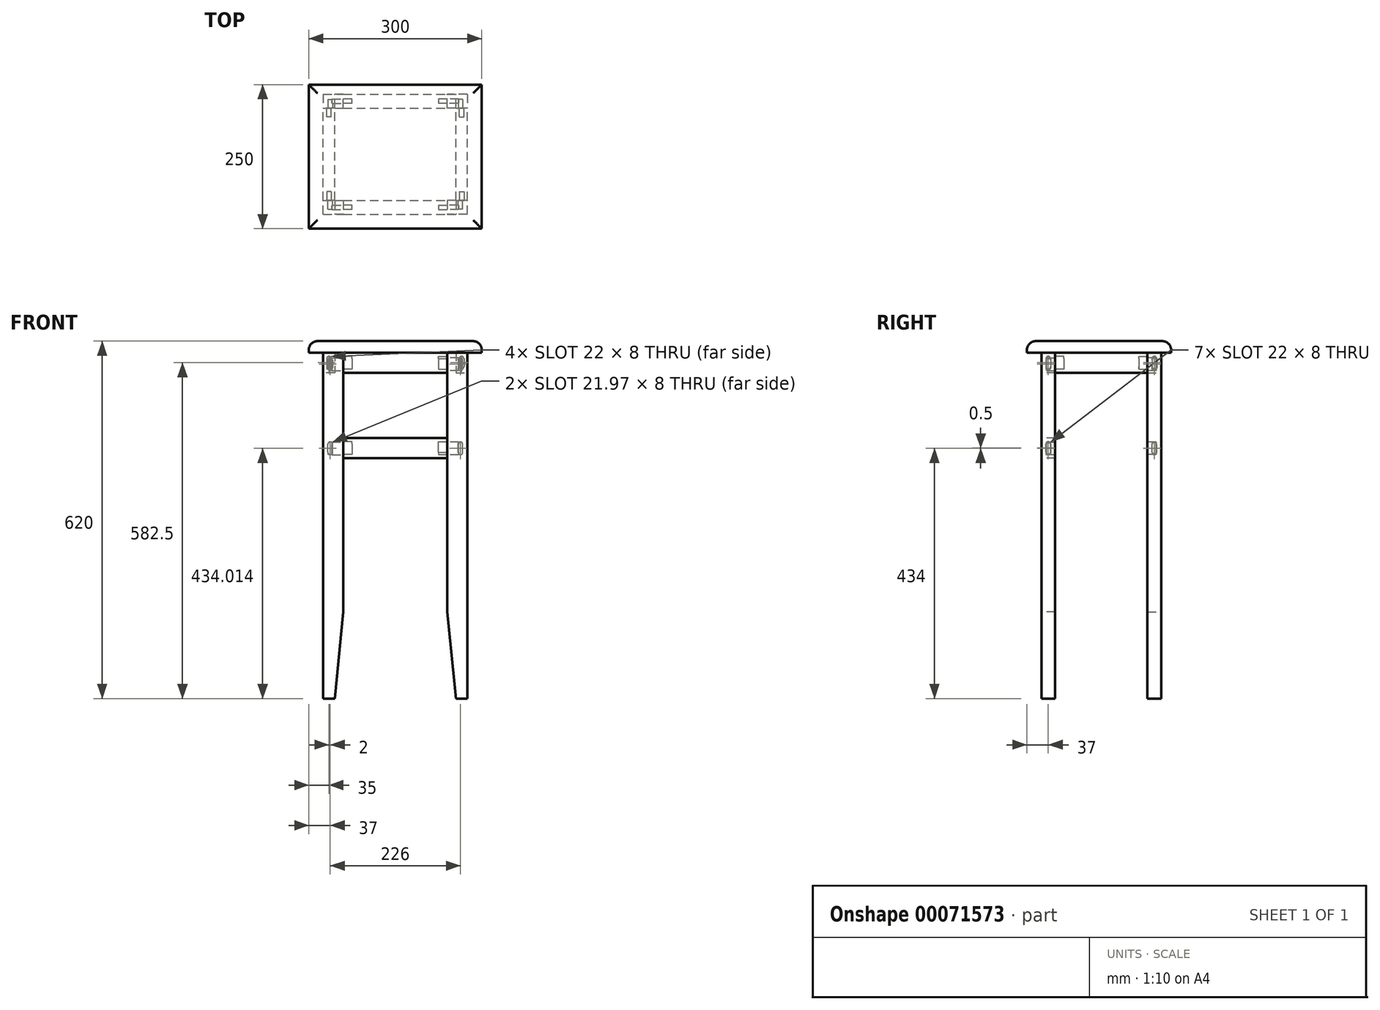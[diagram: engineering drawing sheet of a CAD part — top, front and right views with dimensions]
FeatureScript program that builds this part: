
annotation { "Feature Type Name" : "Feature", "Feature Type Description" : "" }
export const myFeature = defineFeature(function(context is Context, id is Id, definition is map)
    precondition{}
    {
        {
            var Q0;
            Q0=qCreatedBy(makeId("Top.planeOp"),FACE);
            var sketch = newSketch(context, id + "F0", { "sketchPlane" : qUnion([Q0])});
            skLineSegment(sketch, "E0.rect.bottom", {"start": v(125, -100) * mm, "end": v(-125, -100) * mm, "construction": true});
            skLineSegment(sketch, "E0.rect.top", {"start": v(125, 100) * mm, "end": v(-125, 100) * mm, "construction": true});
            skLineSegment(sketch, "E0.rect.left", {"start": v(125, -100) * mm, "end": v(125, 100) * mm, "construction": true});
            skLineSegment(sketch, "E0.rect.right", {"start": v(-125, -100) * mm, "end": v(-125, 100) * mm, "construction": true});
            skPoint(sketch, "E0.rect.middle", {"position": v(0, 0) * mm});
            skLineSegment(sketch, "E1.bottom", {"start": v(-125, -100) * mm, "end": v(-90, -100) * mm});
            skLineSegment(sketch, "E1.top", {"start": v(-125, -76) * mm, "end": v(-90, -76) * mm});
            skLineSegment(sketch, "E1.left", {"start": v(-125, -100) * mm, "end": v(-125, -76) * mm});
            skLineSegment(sketch, "E1.right", {"start": v(-90, -100) * mm, "end": v(-90, -76) * mm});
            skSolve(sketch);
        }
        {
            var Q0;
            Q0=makeQuery(id+"F0.imprint","IMPRINT",FACE,{"disambiguationData":[TD([[makeQuery(id+"F0.imprint","IMPRINT",EDGE,{"derivedFrom":sQuery(id+"F0.wireOp",EDGE,"E1.bottom")}),1.0]])]});
            extrude(context, id + "F1", {"entities" : qUnion([Q0]), "depth" : 600 * mm});
        }
        {
            var Q0;
            Q0=makeQuery(id+"F1.opExtrude","SWEPT_FACE",FACE,{"disambiguationData":[OSD([sQuery(id+"F0.wireOp",EDGE,"E1.right")])]});
            var sketch = newSketch(context, id + "F2", { "sketchPlane" : qUnion([Q0])});
            skLineSegment(sketch, "E2", {"start": v(-88, 508.7) * mm, "end": v(-88, 39.07) * mm, "construction": true});
            skPoint(sketch, "E2.startSnap0", {"position": v(-88, 600) * mm});
            skLineSegment(sketch, "E3.rect.left", {"start": v(-84, 587) * mm, "end": v(-84, 573) * mm});
            skLineSegment(sketch, "E3.rect.right", {"start": v(-92, 587) * mm, "end": v(-92, 573) * mm});
            skLineSegment(sketch, "E4.rect.left", {"start": v(-84, 427) * mm, "end": v(-84, 441) * mm});
            skLineSegment(sketch, "E4.rect.right", {"start": v(-92, 427) * mm, "end": v(-92, 441) * mm});
            skArc(sketch, "E5", {"start": v(-84, 587) * mm, "mid": v(-88, 591) * mm, "end": v(-92, 587) * mm});
            skArc(sketch, "E6", {"start": v(-92, 573) * mm, "mid": v(-88, 569) * mm, "end": v(-84, 573) * mm});
            skArc(sketch, "E7", {"start": v(-84, 441) * mm, "mid": v(-88, 445) * mm, "end": v(-92, 441) * mm});
            skArc(sketch, "E8", {"start": v(-92, 427) * mm, "mid": v(-88, 423) * mm, "end": v(-84, 427) * mm});
            skLineSegment(sketch, "E9", {"start": v(-106.49, 580) * mm, "end": v(-71.34, 580) * mm, "construction": true});
            skLineSegment(sketch, "E10", {"start": v(-106.75, 435) * mm, "end": v(-68.74, 435) * mm, "construction": true});
            skSolve(sketch);
        }
        {
            var Q0;
            Q0 = qSketchRegion(id + "F2", true);
            extrude(context, id + "F3", {"entities" : qUnion([Q0]), "operationType" : NewBodyOperationType.REMOVE, "oppositeDirection" : true, "depth" : 20 * mm});
        }
        {
            var Q0;
            Q0=makeQuery(id+"F1.opExtrude","SWEPT_FACE",FACE,{"disambiguationData":[OSD([sQuery(id+"F0.wireOp",EDGE,"E1.top")])]});
            var sketch = newSketch(context, id + "F4", { "sketchPlane" : qUnion([Q0])});
            skLineSegment(sketch, "E11.rect.left", {"start": v(117, 573) * mm, "end": v(117, 587) * mm});
            skLineSegment(sketch, "E11.rect.right", {"start": v(109, 573) * mm, "end": v(109, 587) * mm});
            skLineSegment(sketch, "E12.rect.left", {"start": v(117, 427.03) * mm, "end": v(117, 441) * mm});
            skLineSegment(sketch, "E12.rect.right", {"start": v(109, 427.03) * mm, "end": v(109, 441) * mm});
            skPoint(sketch, "E12.rect.middle", {"position": v(113, 209.46) * mm});
            skLineSegment(sketch, "E13", {"start": v(108.28, 216) * mm, "end": v(122.23, 216) * mm, "construction": true});
            skLineSegment(sketch, "E14", {"start": v(106.01, 202.03) * mm, "end": v(120.41, 202.03) * mm, "construction": true});
            skLineSegment(sketch, "E15", {"start": v(113, 153.12) * mm, "end": v(113, 125.08) * mm, "construction": true});
            skPoint(sketch, "E15.startSnap0", {"position": v(113, 220.44) * mm});
            skArc(sketch, "E16", {"start": v(117, 441) * mm, "mid": v(113, 445) * mm, "end": v(109, 441) * mm});
            skArc(sketch, "E17", {"start": v(109, 427.03) * mm, "mid": v(113, 423.03) * mm, "end": v(117, 427.03) * mm});
            skPoint(sketch, "E18.orphan", {"position": v(109, 220) * mm});
            skPoint(sketch, "E19.orphan", {"position": v(117, 220.89) * mm});
            skPoint(sketch, "E20.orphan", {"position": v(109, 198.03) * mm});
            skPoint(sketch, "E21.orphan", {"position": v(117, 198.92) * mm});
            skLineSegment(sketch, "E22", {"start": v(107.16, 587) * mm, "end": v(122.33, 587) * mm, "construction": true});
            skLineSegment(sketch, "E23", {"start": v(105.5, 573) * mm, "end": v(120.8, 573) * mm, "construction": true});
            skArc(sketch, "E24", {"start": v(117, 587) * mm, "mid": v(113, 591) * mm, "end": v(109, 587) * mm});
            skArc(sketch, "E25", {"start": v(109, 573) * mm, "mid": v(113, 569) * mm, "end": v(117, 573) * mm});
            skPoint(sketch, "E26.orphan", {"position": v(117, 691) * mm});
            skPoint(sketch, "E27.orphan", {"position": v(117, 669) * mm});
            skSolve(sketch);
        }
        {
            var Q0;
            Q0 = qSketchRegion(id + "F4", true);
            extrude(context, id + "F5", {"entities" : qUnion([Q0]), "operationType" : NewBodyOperationType.REMOVE, "oppositeDirection" : true, "depth" : 15 * mm});
        }
        {
            var Q0;
            Q0=makeQuery(id+"F1.opExtrude","SWEPT_FACE",FACE,{"disambiguationData":[OSD([sQuery(id+"F0.wireOp",EDGE,"E1.bottom")])]});
            var sketch = newSketch(context, id + "F6", { "sketchPlane" : qUnion([Q0])});
            skLineSegment(sketch, "E28", {"start": v(-152.4, 150) * mm, "end": v(-55.36, 150) * mm, "construction": true});
            skLineSegment(sketch, "E29", {"start": v(-105, 80.32) * mm, "end": v(-105, -8.45) * mm, "construction": true});
            skLineSegment(sketch, "E30", {"start": v(-90, 150) * mm, "end": v(-105, 0) * mm});
            skLineSegment(sketch, "E31", {"start": v(-105, 0) * mm, "end": v(-90, 0) * mm});
            skLineSegment(sketch, "E32", {"start": v(-90, 0) * mm, "end": v(-90, 150) * mm});
            skSolve(sketch);
        }
        {
            var Q0;
            Q0=makeQuery(id+"F6.imprint","IMPRINT",FACE,{"disambiguationData":[TD([[makeQuery(id+"F6.imprint","IMPRINT",EDGE,{"derivedFrom":sQuery(id+"F6.wireOp",EDGE,"E30")}),1.0]])]});
            extrude(context, id + "F7", {"entities" : qUnion([Q0]), "operationType" : NewBodyOperationType.REMOVE, "endBound" : BoundingType.THROUGH_ALL, "oppositeDirection" : true, "depth" : 25 * mm});
        }
        {
            var Q0;
            Q0=makeQuery(id+"F1.opExtrude","SWEPT_BODY",BODY,{"disambiguationData":[OSD([sQuery(id+"F0.wireOp",EDGE,"E1.bottom"),sQuery(id+"F0.wireOp",EDGE,"E1.top"),sQuery(id+"F0.wireOp",EDGE,"E1.left"),sQuery(id+"F0.wireOp",EDGE,"E1.right")])]});
            var Q1;
            Q1=makeQuery(id+"F1.opExtrude","SWEPT_FACE",FACE,{"disambiguationData":[OSD([sQuery(id+"F0.wireOp",EDGE,"E1.top")])]});
            mirror(context, id + "F8", {"entities" : qUnion([Q0]), "mirrorPlane" : qUnion([Q1])});
        }
        {
            var Q0;
            Q0=makeQuery(id+"F8.opPattern","COPY",BODY,{"derivedFrom":makeQuery(id+"F1.opExtrude","SWEPT_BODY",BODY,{"disambiguationData":[OSD([sQuery(id+"F0.wireOp",EDGE,"E1.bottom"),sQuery(id+"F0.wireOp",EDGE,"E1.top"),sQuery(id+"F0.wireOp",EDGE,"E1.left"),sQuery(id+"F0.wireOp",EDGE,"E1.right")])]}),"instanceName":"1"});
            transform(context, id + "F9", {"entities" : qUnion([Q0]), "transformType" : TransformType.TRANSLATION_3D, "dx" : 0 * mm, "dy" : 160 * mm, "dz" : 0 * mm, "makeCopy" : false});
        }
        {
            var Q0;
            Q0=makeQuery(id+"F1.opExtrude","SWEPT_BODY",BODY,{"disambiguationData":[OSD([sQuery(id+"F0.wireOp",EDGE,"E1.bottom"),sQuery(id+"F0.wireOp",EDGE,"E1.top"),sQuery(id+"F0.wireOp",EDGE,"E1.left"),sQuery(id+"F0.wireOp",EDGE,"E1.right")])]});
            var Q1;
            Q1=makeQuery(id+"F1.opExtrude","SWEPT_FACE",FACE,{"disambiguationData":[OSD([sQuery(id+"F0.wireOp",EDGE,"E1.right")])]});
            mirror(context, id + "F10", {"entities" : qUnion([Q0]), "mirrorPlane" : qUnion([Q1])});
        }
        {
            var Q0;
            Q0=makeQuery(id+"F8.opPattern","COPY",BODY,{"derivedFrom":makeQuery(id+"F1.opExtrude","SWEPT_BODY",BODY,{"disambiguationData":[OSD([sQuery(id+"F0.wireOp",EDGE,"E1.bottom"),sQuery(id+"F0.wireOp",EDGE,"E1.top"),sQuery(id+"F0.wireOp",EDGE,"E1.left"),sQuery(id+"F0.wireOp",EDGE,"E1.right")])]}),"instanceName":"1"});
            var Q1;
            Q1=makeQuery(id+"F8.opPattern","COPY",FACE,{"derivedFrom":makeQuery(id+"F1.opExtrude","SWEPT_FACE",FACE,{"disambiguationData":[OSD([sQuery(id+"F0.wireOp",EDGE,"E1.right")])]}),"instanceName":"1"});
            mirror(context, id + "F11", {"entities" : qUnion([Q0]), "mirrorPlane" : qUnion([Q1])});
        }
        {
            var Q0;
            Q0=makeQuery(id+"F10.opPattern","COPY",BODY,{"derivedFrom":makeQuery(id+"F1.opExtrude","SWEPT_BODY",BODY,{"disambiguationData":[OSD([sQuery(id+"F0.wireOp",EDGE,"E1.bottom"),sQuery(id+"F0.wireOp",EDGE,"E1.top"),sQuery(id+"F0.wireOp",EDGE,"E1.left"),sQuery(id+"F0.wireOp",EDGE,"E1.right")])]}),"instanceName":"1"});
            transform(context, id + "F12", {"entities" : qUnion([Q0]), "transformType" : TransformType.TRANSLATION_3D, "dx" : 180 * mm, "dy" : 0 * mm, "dz" : 0 * mm, "makeCopy" : false});
        }
        {
            var Q0;
            Q0=makeQuery(id+"F11.opPattern","COPY",BODY,{"derivedFrom":makeQuery(id+"F8.opPattern","COPY",BODY,{"derivedFrom":makeQuery(id+"F1.opExtrude","SWEPT_BODY",BODY,{"disambiguationData":[OSD([sQuery(id+"F0.wireOp",EDGE,"E1.bottom"),sQuery(id+"F0.wireOp",EDGE,"E1.top"),sQuery(id+"F0.wireOp",EDGE,"E1.left"),sQuery(id+"F0.wireOp",EDGE,"E1.right")])]}),"instanceName":"1"}),"instanceName":"1"});
            transform(context, id + "F13", {"entities" : qUnion([Q0]), "transformType" : TransformType.TRANSLATION_3D, "dx" : 180 * mm, "dy" : 0 * mm, "dz" : 0 * mm, "makeCopy" : false});
        }
        {
            var Q0;
            Q0=makeQuery(id+"F1.opExtrude","SWEPT_FACE",FACE,{"disambiguationData":[OSD([sQuery(id+"F0.wireOp",EDGE,"E1.bottom")])]});
            var sketch = newSketch(context, id + "F14", { "sketchPlane" : qUnion([Q0])});
            skLineSegment(sketch, "E33", {"start": v(-90, 600) * mm, "end": v(90, 600) * mm});
            skLineSegment(sketch, "E34", {"start": v(-90, 600) * mm, "end": v(-90, 565) * mm});
            skLineSegment(sketch, "E35", {"start": v(-90, 565) * mm, "end": v(90, 565) * mm});
            skLineSegment(sketch, "E36", {"start": v(90, 565) * mm, "end": v(90, 600) * mm});
            skSolve(sketch);
        }
        {
            var Q0;
            Q0=makeQuery(id+"F14.imprint","IMPRINT",FACE,{"disambiguationData":[TD([[makeQuery(id+"F14.imprint","IMPRINT",EDGE,{"derivedFrom":sQuery(id+"F14.wireOp",EDGE,"E33")}),-1.0]])]});
            extrude(context, id + "F15", {"entities" : qUnion([Q0]), "oppositeDirection" : true, "depth" : 24 * mm});
        }
        {
            var Q0;
            Q0=makeQuery(id+"F15.opExtrude","SWEPT_FACE",FACE,{"disambiguationData":[OSD([sQuery(id+"F14.wireOp",EDGE,"E36")])]});
            var sketch = newSketch(context, id + "F16", { "sketchPlane" : qUnion([Q0])});
            skLineSegment(sketch, "E37.rect.left", {"start": v(-84, 589.67) * mm, "end": v(-84, 575.47) * mm});
            skLineSegment(sketch, "E37.rect.right", {"start": v(-92, 589.67) * mm, "end": v(-92, 575.47) * mm});
            skPoint(sketch, "E37.rect.middle", {"position": v(-88, 582.5) * mm});
            skLineSegment(sketch, "E38", {"start": v(-96.52, 589.33) * mm, "end": v(-79.54, 589.33) * mm, "construction": true});
            skLineSegment(sketch, "E39", {"start": v(-96.23, 575.53) * mm, "end": v(-79.5, 575.53) * mm, "construction": true});
            skLineSegment(sketch, "E40", {"start": v(-88, 597.3) * mm, "end": v(-88, 566.6) * mm, "construction": true});
            skPoint(sketch, "E40.startSnap0", {"position": v(-88, 593.5) * mm});
            skArc(sketch, "E41", {"start": v(-92, 575.53) * mm, "mid": v(-88, 571.5) * mm, "end": v(-84, 575.53) * mm});
            skPoint(sketch, "E41.first.point", {"position": v(-92, 575.53) * mm});
            skPoint(sketch, "E41.second.point", {"position": v(-88, 571.5) * mm});
            skPoint(sketch, "E41.third.point", {"position": v(-84, 575.53) * mm});
            skArc(sketch, "E42", {"start": v(-84, 589.33) * mm, "mid": v(-88, 593.5) * mm, "end": v(-92, 589.33) * mm});
            skPoint(sketch, "E42.first.point", {"position": v(-92, 589.33) * mm});
            skPoint(sketch, "E42.third.point", {"position": v(-84, 589.33) * mm});
            skPoint(sketch, "E43.orphan", {"position": v(-84, 593.5) * mm});
            skPoint(sketch, "E44.orphan", {"position": v(-92, 593.5) * mm});
            skPoint(sketch, "E45.orphan", {"position": v(-92, 571.5) * mm});
            skPoint(sketch, "E46.orphan", {"position": v(-84, 571.5) * mm});
            skSolve(sketch);
        }
        {
            var Q0;
            {var subQ0=sQuery(id+"F16.wireOp",EDGE,"E42");var subQ6=sQuery(id+"F16.wireOp",EDGE,"E37.rect.left");var subQ10=makeQuery(id+"F16.imprint","INTERSECT",VERTEX,{"disambiguationData":[OD(0.0)],"derivedFrom":[subQ6,subQ0]});Q0=makeQuery(id+"F16.imprint","IMPRINT",FACE,{"disambiguationData":[TD([[makeQuery(id+"F16.imprint","IMPRINT",EDGE,{"disambiguationData":[TD([[subQ10,-1.0]])],"derivedFrom":subQ6}),-1.0]])]});}
            extrude(context, id + "F17", {"entities" : qUnion([Q0]), "operationType" : NewBodyOperationType.REMOVE, "oppositeDirection" : true, "depth" : 15 * mm});
        }
        {
            var Q0;
            Q0=makeQuery(id+"F1.opExtrude","SWEPT_FACE",FACE,{"disambiguationData":[OSD([sQuery(id+"F0.wireOp",EDGE,"E1.left")])]});
            var sketch = newSketch(context, id + "F18", { "sketchPlane" : qUnion([Q0])});
            skLineSegment(sketch, "E47.bottom", {"start": v(76, 600) * mm, "end": v(-84, 600) * mm});
            skLineSegment(sketch, "E47.top", {"start": v(76, 565) * mm, "end": v(-84, 565) * mm});
            skLineSegment(sketch, "E47.left", {"start": v(76, 600) * mm, "end": v(76, 565) * mm});
            skLineSegment(sketch, "E47.right", {"start": v(-84, 600) * mm, "end": v(-84, 565) * mm});
            skSolve(sketch);
        }
        {
            var Q0;
            Q0=makeQuery(id+"F18.imprint","IMPRINT",FACE,{"disambiguationData":[TD([[makeQuery(id+"F18.imprint","IMPRINT",EDGE,{"derivedFrom":sQuery(id+"F18.wireOp",EDGE,"E47.bottom")}),1.0]])]});
            extrude(context, id + "F19", {"entities" : qUnion([Q0]), "oppositeDirection" : true, "depth" : 27.5 * mm});
        }
        {
            var Q0;
            Q0=makeQuery(id+"F19.opExtrude","CAP_FACE",FACE,{"disambiguationData":[OSD([sQuery(id+"F18.wireOp",EDGE,"E47.bottom"),sQuery(id+"F18.wireOp",EDGE,"E47.top"),sQuery(id+"F18.wireOp",EDGE,"E47.left"),sQuery(id+"F18.wireOp",EDGE,"E47.right")])],"isStart":true});
            extrude(context, id + "F20", {"entities" : qUnion([Q0]), "operationType" : NewBodyOperationType.REMOVE, "oppositeDirection" : true, "depth" : 7.5 * mm});
        }
        {
            var Q0;
            Q0=makeQuery(id+"F15.opExtrude","SWEPT_BODY",BODY,{"disambiguationData":[OSD([sQuery(id+"F14.wireOp",EDGE,"E33"),sQuery(id+"F14.wireOp",EDGE,"E34"),sQuery(id+"F14.wireOp",EDGE,"E35"),sQuery(id+"F14.wireOp",EDGE,"E36")])]});
            var Q1;
            Q1=makeQuery(id+"F15.opExtrude","CAP_FACE",FACE,{"disambiguationData":[OSD([sQuery(id+"F14.wireOp",EDGE,"E33"),sQuery(id+"F14.wireOp",EDGE,"E34"),sQuery(id+"F14.wireOp",EDGE,"E35"),sQuery(id+"F14.wireOp",EDGE,"E36")])],"isStart":false});
            mirror(context, id + "F21", {"entities" : qUnion([Q0]), "mirrorPlane" : qUnion([Q1])});
        }
        {
            var Q0;
            Q0=makeQuery(id+"F21.opPattern","COPY",BODY,{"derivedFrom":makeQuery(id+"F15.opExtrude","SWEPT_BODY",BODY,{"disambiguationData":[OSD([sQuery(id+"F14.wireOp",EDGE,"E33"),sQuery(id+"F14.wireOp",EDGE,"E34"),sQuery(id+"F14.wireOp",EDGE,"E35"),sQuery(id+"F14.wireOp",EDGE,"E36")])]}),"instanceName":"1"});
            transform(context, id + "F22", {"entities" : qUnion([Q0]), "transformType" : TransformType.TRANSLATION_3D, "dx" : 0 * mm, "dy" : 160 * mm, "dz" : 0 * mm, "makeCopy" : false});
        }
        {
            var Q0;
            Q0=makeQuery(id+"F19.opExtrude","SWEPT_BODY",BODY,{"disambiguationData":[OSD([sQuery(id+"F18.wireOp",EDGE,"E47.bottom"),sQuery(id+"F18.wireOp",EDGE,"E47.top"),sQuery(id+"F18.wireOp",EDGE,"E47.left"),sQuery(id+"F18.wireOp",EDGE,"E47.right")])]});
            transform(context, id + "F23", {"entities" : qUnion([Q0]), "transformType" : TransformType.TRANSLATION_3D, "dx" : -7.5 * mm, "dy" : 0 * mm, "dz" : 0 * mm, "makeCopy" : false});
        }
        {
            var Q0;
            Q0=makeQuery(id+"F19.opExtrude","SWEPT_FACE",FACE,{"disambiguationData":[OSD([sQuery(id+"F18.wireOp",EDGE,"E47.left")])]});
            var sketch = newSketch(context, id + "F24", { "sketchPlane" : qUnion([Q0])});
            skLineSegment(sketch, "E48.rect.left", {"start": v(-119, 589.5) * mm, "end": v(-119, 575.5) * mm});
            skLineSegment(sketch, "E48.rect.right", {"start": v(-111, 589.5) * mm, "end": v(-111, 575.5) * mm});
            skPoint(sketch, "E48.rect.middle", {"position": v(-115, 582.5) * mm});
            skLineSegment(sketch, "E49", {"start": v(-115, 597.87) * mm, "end": v(-115, 566.96) * mm, "construction": true});
            skPoint(sketch, "E49.startSnap0", {"position": v(-115, 593.5) * mm});
            skLineSegment(sketch, "E50", {"start": v(-123.95, 589.5) * mm, "end": v(-106.1, 589.5) * mm, "construction": true});
            skLineSegment(sketch, "E51", {"start": v(-123.85, 575.5) * mm, "end": v(-106.12, 575.5) * mm, "construction": true});
            skArc(sketch, "E52", {"start": v(-111, 589.5) * mm, "mid": v(-115, 593.5) * mm, "end": v(-119, 589.5) * mm});
            skPoint(sketch, "E52.first.point", {"position": v(-119, 589.5) * mm});
            skPoint(sketch, "E52.second.point", {"position": v(-111, 589.5) * mm});
            skArc(sketch, "E53", {"start": v(-119, 575.5) * mm, "mid": v(-115, 571.5) * mm, "end": v(-111, 575.5) * mm});
            skPoint(sketch, "E53.first.point", {"position": v(-119, 575.5) * mm});
            skPoint(sketch, "E53.second.point", {"position": v(-111, 575.5) * mm});
            skPoint(sketch, "E53.third.point", {"position": v(-115, 571.5) * mm});
            skPoint(sketch, "E54.orphan", {"position": v(-119, 593.5) * mm});
            skPoint(sketch, "E55.orphan", {"position": v(-111, 593.5) * mm});
            skPoint(sketch, "E56.orphan", {"position": v(-119, 571.5) * mm});
            skPoint(sketch, "E57.orphan", {"position": v(-111, 571.5) * mm});
            skSolve(sketch);
        }
        {
            var Q0;
            Q0=makeQuery(id+"F19.opExtrude","SWEPT_FACE",FACE,{"disambiguationData":[OSD([sQuery(id+"F18.wireOp",EDGE,"E47.right")])]});
            var sketch = newSketch(context, id + "F25", { "sketchPlane" : qUnion([Q0])});
            skLineSegment(sketch, "E58.rect.left", {"start": v(111, 589.5) * mm, "end": v(111, 575.5) * mm});
            skLineSegment(sketch, "E58.rect.right", {"start": v(119, 589.5) * mm, "end": v(119, 575.5) * mm});
            skPoint(sketch, "E58.rect.middle", {"position": v(115, 582.5) * mm});
            skPoint(sketch, "E58.rect.middle.positionSnap0", {"position": v(115, 600) * mm});
            skPoint(sketch, "E58.rect.middle.positionSnap1", {"position": v(125, 582.5) * mm});
            skPoint(sketch, "E58.rect.centerSnap0", {"position": v(115, 600) * mm});
            skPoint(sketch, "E58.rect.centerSnap1", {"position": v(125, 582.5) * mm});
            skLineSegment(sketch, "E59", {"start": v(115, 503.56) * mm, "end": v(115, 561.97) * mm, "construction": true});
            skPoint(sketch, "E59.endSnap0", {"position": v(115, 565) * mm});
            skLineSegment(sketch, "E60", {"start": v(106.87, 589.5) * mm, "end": v(123.6, 589.5) * mm, "construction": true});
            skLineSegment(sketch, "E61", {"start": v(106.56, 575.5) * mm, "end": v(122.76, 575.5) * mm, "construction": true});
            skArc(sketch, "E62", {"start": v(119, 589.5) * mm, "mid": v(115, 593.5) * mm, "end": v(111, 589.5) * mm});
            skPoint(sketch, "E62.first.point", {"position": v(111, 589.5) * mm});
            skPoint(sketch, "E62.second.point", {"position": v(115, 593.5) * mm});
            skPoint(sketch, "E62.third.point", {"position": v(119, 589.5) * mm});
            skArc(sketch, "E63", {"start": v(111, 575.5) * mm, "mid": v(115, 571.5) * mm, "end": v(119, 575.5) * mm});
            skPoint(sketch, "E63.first.point", {"position": v(111, 575.5) * mm});
            skPoint(sketch, "E63.second.point", {"position": v(115.23, 571.5) * mm});
            skPoint(sketch, "E63.second.point.positionSnap0", {"position": v(115.23, 589.5) * mm});
            skPoint(sketch, "E63.third.point", {"position": v(119, 575.5) * mm});
            skPoint(sketch, "E64.orphan", {"position": v(111, 593.5) * mm});
            skPoint(sketch, "E65.orphan", {"position": v(119, 593.5) * mm});
            skPoint(sketch, "E66.orphan", {"position": v(111, 571.5) * mm});
            skPoint(sketch, "E67.orphan", {"position": v(119, 571.5) * mm});
            skSolve(sketch);
        }
        {
            var Q0;
            Q0=makeQuery(id+"F15.opExtrude","SWEPT_BODY",BODY,{"disambiguationData":[OSD([sQuery(id+"F14.wireOp",EDGE,"E33"),sQuery(id+"F14.wireOp",EDGE,"E34"),sQuery(id+"F14.wireOp",EDGE,"E35"),sQuery(id+"F14.wireOp",EDGE,"E36")])]});
            var Q1;
            Q1=makeQuery(id+"F15.opExtrude","SWEPT_FACE",FACE,{"disambiguationData":[OSD([sQuery(id+"F14.wireOp",EDGE,"E35")])]});
            mirror(context, id + "F26", {"entities" : qUnion([Q0]), "mirrorPlane" : qUnion([Q1])});
        }
        {
            var Q0;
            Q0=makeQuery(id+"F26.opPattern","COPY",BODY,{"derivedFrom":makeQuery(id+"F15.opExtrude","SWEPT_BODY",BODY,{"disambiguationData":[OSD([sQuery(id+"F14.wireOp",EDGE,"E33"),sQuery(id+"F14.wireOp",EDGE,"E34"),sQuery(id+"F14.wireOp",EDGE,"E35"),sQuery(id+"F14.wireOp",EDGE,"E36")])]}),"instanceName":"1"});
            transform(context, id + "F27", {"entities" : qUnion([Q0]), "transformType" : TransformType.TRANSLATION_3D, "dx" : 0 * mm, "dy" : 0 * mm, "dz" : -338 * mm, "makeCopy" : false});
        }
        {
            var Q0;
            Q0=makeQuery(id+"F21.opPattern","COPY",FACE,{"derivedFrom":makeQuery(id+"F15.opExtrude","SWEPT_FACE",FACE,{"disambiguationData":[OSD([sQuery(id+"F14.wireOp",EDGE,"E36")])]}),"instanceName":"1"});
            var sketch = newSketch(context, id + "F28", { "sketchPlane" : qUnion([Q0])});
            skLineSegment(sketch, "E68", {"start": v(96, 505.4) * mm, "end": v(96, 455.46) * mm, "construction": true});
            skPoint(sketch, "E68.startSnap0", {"position": v(96, 600) * mm});
            skLineSegment(sketch, "E69", {"start": v(76.16, 582.5) * mm, "end": v(106.38, 582.5) * mm, "construction": true});
            skPoint(sketch, "E69.startSnap0", {"position": v(84, 582.5) * mm});
            skLineSegment(sketch, "E70.rect.left", {"start": v(100, 589.5) * mm, "end": v(100, 575.5) * mm});
            skLineSegment(sketch, "E70.rect.right", {"start": v(92, 589.5) * mm, "end": v(92, 575.5) * mm});
            skPoint(sketch, "E70.rect.middle", {"position": v(96, 582.5) * mm});
            skLineSegment(sketch, "E71", {"start": v(88.07, 589.5) * mm, "end": v(104.42, 589.5) * mm, "construction": true});
            skLineSegment(sketch, "E72", {"start": v(88.34, 575.5) * mm, "end": v(103.44, 575.5) * mm, "construction": true});
            skArc(sketch, "E73", {"start": v(92, 575.5) * mm, "mid": v(96, 571.5) * mm, "end": v(100, 575.5) * mm});
            skPoint(sketch, "E73.first.point", {"position": v(92, 575.5) * mm});
            skPoint(sketch, "E73.second.point", {"position": v(96, 571.5) * mm});
            skPoint(sketch, "E73.third.point", {"position": v(100, 575.5) * mm});
            skArc(sketch, "E74", {"start": v(100, 589.5) * mm, "mid": v(96, 593.5) * mm, "end": v(92, 589.5) * mm});
            skPoint(sketch, "E74.first.point", {"position": v(92, 589.5) * mm});
            skPoint(sketch, "E74.first.point.positionSnap0", {"position": v(96.25, 589.5) * mm});
            skPoint(sketch, "E74.second.point", {"position": v(96, 593.5) * mm});
            skPoint(sketch, "E74.third.point", {"position": v(100, 589.5) * mm});
            skPoint(sketch, "E74.third.point.positionSnap0", {"position": v(96.25, 589.5) * mm});
            skPoint(sketch, "E75.orphan", {"position": v(92, 593.5) * mm});
            skPoint(sketch, "E76.orphan", {"position": v(100, 593.5) * mm});
            skPoint(sketch, "E77.orphan", {"position": v(92, 571.5) * mm});
            skPoint(sketch, "E78.orphan", {"position": v(100, 571.5) * mm});
            skSolve(sketch);
        }
        {
            var Q0;
            Q0=makeQuery(id+"F28.imprint","IMPRINT",FACE,{"disambiguationData":[TD([[makeQuery(id+"F28.imprint","IMPRINT",EDGE,{"derivedFrom":sQuery(id+"F28.wireOp",EDGE,"E70.rect.left")}),-1.0]])]});
            extrude(context, id + "F29", {"entities" : qUnion([Q0]), "operationType" : NewBodyOperationType.REMOVE, "oppositeDirection" : true, "depth" : 15 * mm});
        }
        {
            var Q0;
            Q0=makeQuery(id+"F21.opPattern","COPY",FACE,{"derivedFrom":makeQuery(id+"F15.opExtrude","SWEPT_FACE",FACE,{"disambiguationData":[OSD([sQuery(id+"F14.wireOp",EDGE,"E34")])]}),"instanceName":"1"});
            var sketch = newSketch(context, id + "F30", { "sketchPlane" : qUnion([Q0])});
            skLineSegment(sketch, "E79", {"start": v(-96, 504.53) * mm, "end": v(-96, 460.47) * mm, "construction": true});
            skPoint(sketch, "E79.startSnap0", {"position": v(-96, 600) * mm});
            skLineSegment(sketch, "E80", {"start": v(-104.7, 582.5) * mm, "end": v(-71.23, 582.5) * mm, "construction": true});
            skPoint(sketch, "E80.startSnap0", {"position": v(-108, 582.5) * mm});
            skLineSegment(sketch, "E81.rect.left", {"start": v(-92, 589.5) * mm, "end": v(-92, 575.5) * mm});
            skLineSegment(sketch, "E81.rect.right", {"start": v(-100, 589.5) * mm, "end": v(-100, 575.5) * mm});
            skPoint(sketch, "E81.rect.middle", {"position": v(-96, 582.5) * mm});
            skLineSegment(sketch, "E82", {"start": v(-104.3, 589.5) * mm, "end": v(-87.4, 589.5) * mm, "construction": true});
            skLineSegment(sketch, "E83", {"start": v(-104.03, 575.5) * mm, "end": v(-87.22, 575.5) * mm, "construction": true});
            skArc(sketch, "E84", {"start": v(-92, 589.5) * mm, "mid": v(-96, 593.5) * mm, "end": v(-100, 589.5) * mm});
            skPoint(sketch, "E84.first.point", {"position": v(-100, 589.5) * mm});
            skPoint(sketch, "E84.second.point", {"position": v(-96, 593.5) * mm});
            skPoint(sketch, "E84.third.point", {"position": v(-92, 589.5) * mm});
            skArc(sketch, "E85", {"start": v(-100, 575.5) * mm, "mid": v(-96, 571.5) * mm, "end": v(-92, 575.5) * mm});
            skPoint(sketch, "E85.first.point", {"position": v(-100, 575.5) * mm});
            skPoint(sketch, "E85.second.point", {"position": v(-96, 571.5) * mm});
            skPoint(sketch, "E85.third.point", {"position": v(-92, 575.5) * mm});
            skPoint(sketch, "E86.orphan", {"position": v(-100, 593.5) * mm});
            skPoint(sketch, "E87.orphan", {"position": v(-92, 593.5) * mm});
            skPoint(sketch, "E88.orphan", {"position": v(-92, 571.5) * mm});
            skPoint(sketch, "E89.orphan", {"position": v(-100, 571.5) * mm});
            skSolve(sketch);
        }
        {
            var Q0;
            Q0=makeQuery(id+"F30.imprint","IMPRINT",FACE,{"disambiguationData":[TD([[makeQuery(id+"F30.imprint","IMPRINT",EDGE,{"derivedFrom":sQuery(id+"F30.wireOp",EDGE,"E81.rect.left")}),-1.0]])]});
            extrude(context, id + "F31", {"entities" : qUnion([Q0]), "operationType" : NewBodyOperationType.REMOVE, "oppositeDirection" : true, "depth" : 15 * mm});
        }
        {
            var Q0;
            {var subQ0=sQuery(id+"F16.wireOp",EDGE,"E42");var subQ6=sQuery(id+"F16.wireOp",EDGE,"E37.rect.left");var subQ10=makeQuery(id+"F16.imprint","INTERSECT",VERTEX,{"disambiguationData":[OD(0.0)],"derivedFrom":[subQ6,subQ0]});Q0=makeQuery(id+"F16.imprint","IMPRINT",FACE,{"disambiguationData":[TD([[makeQuery(id+"F16.imprint","IMPRINT",EDGE,{"disambiguationData":[TD([[subQ10,-1.0]])],"derivedFrom":subQ6}),-1.0]])]});}
            extrude(context, id + "F32", {"entities" : qUnion([Q0]), "operationType" : NewBodyOperationType.REMOVE, "oppositeDirection" : true, "depth" : 15 * mm});
        }
        {
            var Q0;
            Q0 = qSketchRegion(id + "F24", true);
            extrude(context, id + "F33", {"entities" : qUnion([Q0]), "operationType" : NewBodyOperationType.REMOVE, "oppositeDirection" : true, "depth" : 15 * mm});
        }
        {
            var Q0;
            Q0 = qSketchRegion(id + "F25", true);
            extrude(context, id + "F34", {"entities" : qUnion([Q0]), "operationType" : NewBodyOperationType.REMOVE, "oppositeDirection" : true, "depth" : 15 * mm});
        }
        {
            var Q0;
            Q0=makeQuery(id+"F19.opExtrude","SWEPT_BODY",BODY,{"disambiguationData":[OSD([sQuery(id+"F18.wireOp",EDGE,"E47.bottom"),sQuery(id+"F18.wireOp",EDGE,"E47.top"),sQuery(id+"F18.wireOp",EDGE,"E47.left"),sQuery(id+"F18.wireOp",EDGE,"E47.right")])]});
            var Q1;
            Q1=makeQuery(id+"F19.opExtrude","CAP_FACE",FACE,{"disambiguationData":[OSD([sQuery(id+"F18.wireOp",EDGE,"E47.bottom"),sQuery(id+"F18.wireOp",EDGE,"E47.top"),sQuery(id+"F18.wireOp",EDGE,"E47.left"),sQuery(id+"F18.wireOp",EDGE,"E47.right")])],"isStart":false});
            mirror(context, id + "F35", {"entities" : qUnion([Q0]), "mirrorPlane" : qUnion([Q1])});
        }
        {
            var Q0;
            Q0=makeQuery(id+"F35.opPattern","COPY",BODY,{"derivedFrom":makeQuery(id+"F19.opExtrude","SWEPT_BODY",BODY,{"disambiguationData":[OSD([sQuery(id+"F18.wireOp",EDGE,"E47.bottom"),sQuery(id+"F18.wireOp",EDGE,"E47.top"),sQuery(id+"F18.wireOp",EDGE,"E47.left"),sQuery(id+"F18.wireOp",EDGE,"E47.right")])]}),"instanceName":"1"});
            transform(context, id + "F36", {"entities" : qUnion([Q0]), "transformType" : TransformType.TRANSLATION_3D, "dx" : 210 * mm, "dy" : 0 * mm, "dz" : 0 * mm, "makeCopy" : false});
        }
        {
            var Q0;
            Q0=makeQuery(id+"F26.opPattern","COPY",FACE,{"derivedFrom":makeQuery(id+"F15.opExtrude","SWEPT_FACE",FACE,{"disambiguationData":[OSD([sQuery(id+"F14.wireOp",EDGE,"E34")])]}),"instanceName":"1"});
            var sketch = newSketch(context, id + "F37", { "sketchPlane" : qUnion([Q0])});
            skLineSegment(sketch, "E90", {"start": v(88, 161.62) * mm, "end": v(88, 117) * mm, "construction": true});
            skPoint(sketch, "E90.startSnap0", {"position": v(88, 227) * mm});
            skLineSegment(sketch, "E91", {"start": v(76.3, 209.5) * mm, "end": v(110.21, 209.5) * mm, "construction": true});
            skPoint(sketch, "E91.startSnap0", {"position": v(76, 209.5) * mm});
            skLineSegment(sketch, "E92.rect.left", {"start": v(92, 216.5) * mm, "end": v(92, 202.5) * mm});
            skLineSegment(sketch, "E92.rect.right", {"start": v(84, 216.5) * mm, "end": v(84, 202.5) * mm});
            skPoint(sketch, "E92.rect.middle", {"position": v(88, 209.5) * mm});
            skPoint(sketch, "E92.rect.middle.positionSnap0", {"position": v(88, 139.31) * mm});
            skPoint(sketch, "E92.rect.centerSnap0", {"position": v(88, 139.31) * mm});
            skLineSegment(sketch, "E93", {"start": v(80.13, 216.5) * mm, "end": v(96.18, 216.5) * mm, "construction": true});
            skLineSegment(sketch, "E94", {"start": v(80.5, 202.5) * mm, "end": v(96.18, 202.5) * mm, "construction": true});
            skArc(sketch, "E95", {"start": v(92, 216.5) * mm, "mid": v(88, 220.5) * mm, "end": v(84, 216.5) * mm});
            skPoint(sketch, "E95.first.point", {"position": v(84, 216.5) * mm});
            skPoint(sketch, "E95.second.point", {"position": v(88, 220.5) * mm});
            skPoint(sketch, "E95.third.point", {"position": v(92, 216.5) * mm});
            skArc(sketch, "E96", {"start": v(84, 202.5) * mm, "mid": v(88, 198.5) * mm, "end": v(92, 202.5) * mm});
            skPoint(sketch, "E96.first.point", {"position": v(84, 202.5) * mm});
            skPoint(sketch, "E96.second.point", {"position": v(88, 198.5) * mm});
            skPoint(sketch, "E96.third.point", {"position": v(92, 202.5) * mm});
            skPoint(sketch, "E97.orphan", {"position": v(84, 220.5) * mm});
            skPoint(sketch, "E98.orphan", {"position": v(92, 220.5) * mm});
            skPoint(sketch, "E99.orphan", {"position": v(84, 198.5) * mm});
            skPoint(sketch, "E100.orphan", {"position": v(92, 198.5) * mm});
            skSolve(sketch);
        }
        {
            var Q0;
            Q0 = qSketchRegion(id + "F37", true);
            extrude(context, id + "F38", {"entities" : qUnion([Q0]), "operationType" : NewBodyOperationType.REMOVE, "oppositeDirection" : true, "depth" : 15 * mm});
        }
        {
            var Q0;
            Q0=makeQuery(id+"F8.opPattern","COPY",FACE,{"derivedFrom":makeQuery(id+"F1.opExtrude","CAP_FACE",FACE,{"disambiguationData":[OSD([sQuery(id+"F0.wireOp",EDGE,"E1.bottom"),sQuery(id+"F0.wireOp",EDGE,"E1.top"),sQuery(id+"F0.wireOp",EDGE,"E1.left"),sQuery(id+"F0.wireOp",EDGE,"E1.right")])],"isStart":false}),"instanceName":"1"});
            var sketch = newSketch(context, id + "F39", { "sketchPlane" : qUnion([Q0])});
            skLineSegment(sketch, "E101.rect.bottom", {"start": v(150, 125) * mm, "end": v(-150, 125) * mm});
            skLineSegment(sketch, "E101.rect.top", {"start": v(150, -125) * mm, "end": v(-150, -125) * mm});
            skLineSegment(sketch, "E101.rect.left", {"start": v(150, 125) * mm, "end": v(150, -125) * mm});
            skLineSegment(sketch, "E101.rect.right", {"start": v(-150, 125) * mm, "end": v(-150, -125) * mm});
            skPoint(sketch, "E101.rect.middle", {"position": v(0, 0) * mm});
            skSolve(sketch);
        }
        {
            var Q0;
            Q0 = qSketchRegion(id + "F39", true);
            extrude(context, id + "F40", {"entities" : qUnion([Q0]), "depth" : 20 * mm});
        }
        {
            var Q0;
            Q0=makeQuery(id+"F40.opExtrude","CAP_EDGE",EDGE,{"disambiguationData":[OSD([sQuery(id+"F39.wireOp",EDGE,"E101.rect.right")])],"isStart":false});
            var Q1;
            Q1=makeQuery(id+"F40.opExtrude","CAP_EDGE",EDGE,{"disambiguationData":[OSD([sQuery(id+"F39.wireOp",EDGE,"E101.rect.top")])],"isStart":false});
            var Q2;
            Q2=makeQuery(id+"F40.opExtrude","CAP_EDGE",EDGE,{"disambiguationData":[OSD([sQuery(id+"F39.wireOp",EDGE,"E101.rect.left")])],"isStart":false});
            var Q3;
            Q3=makeQuery(id+"F40.opExtrude","CAP_EDGE",EDGE,{"disambiguationData":[OSD([sQuery(id+"F39.wireOp",EDGE,"E101.rect.bottom")])],"isStart":false});
            fillet(context, id + "F41", {"entities" : qUnion([Q0, Q1, Q2, Q3]), "radius" : 15 * mm, "tangentPropagation" : true, "allowEdgeOverflow" : false});
        }
        {
            var Q0;
            Q0=makeQuery(id+"F15.opExtrude","SWEPT_FACE",FACE,{"disambiguationData":[OSD([sQuery(id+"F14.wireOp",EDGE,"E34")])]});
            var sketch = newSketch(context, id + "F42", { "sketchPlane" : qUnion([Q0])});
            skLineSegment(sketch, "E102", {"start": v(88, 600) * mm, "end": v(88, 565) * mm, "construction": true});
            skArc(sketch, "E103", {"start": v(92, 589.5) * mm, "mid": v(88, 593.5) * mm, "end": v(84, 589.5) * mm});
            skArc(sketch, "E104", {"start": v(84, 575.5) * mm, "mid": v(88, 571.5) * mm, "end": v(92, 575.5) * mm});
            skLineSegment(sketch, "E105", {"start": v(84, 589.5) * mm, "end": v(84, 575.5) * mm});
            skLineSegment(sketch, "E106", {"start": v(92, 589.5) * mm, "end": v(92, 575.5) * mm});
            skSolve(sketch);
        }
        {
            var Q0;
            Q0 = qSketchRegion(id + "F42", true);
            extrude(context, id + "F43", {"entities" : qUnion([Q0]), "operationType" : NewBodyOperationType.REMOVE, "oppositeDirection" : true, "depth" : 15 * mm});
        }
        {
            var Q0;
            Q0=makeQuery(id+"F26.opPattern","COPY",BODY,{"derivedFrom":makeQuery(id+"F15.opExtrude","SWEPT_BODY",BODY,{"disambiguationData":[OSD([sQuery(id+"F14.wireOp",EDGE,"E33"),sQuery(id+"F14.wireOp",EDGE,"E34"),sQuery(id+"F14.wireOp",EDGE,"E35"),sQuery(id+"F14.wireOp",EDGE,"E36")])]}),"instanceName":"1"});
            transform(context, id + "F44", {"entities" : qUnion([Q0]), "transformType" : TransformType.TRANSLATION_3D, "dx" : 0 * mm, "dy" : 0 * mm, "dz" : 225 * mm, "makeCopy" : false});
        }
    });
